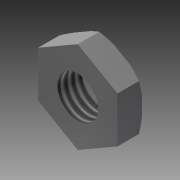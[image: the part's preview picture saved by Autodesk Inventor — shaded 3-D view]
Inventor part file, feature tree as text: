
AUTODESK INVENTOR PART (.ipt)
format: ipt  version: 2013 (Build 170138000, 138)  size: 109,056 bytes
history: native  units: mm
features: sketch x2, other x1, revolve x1, extrude x1, thread x1
ambient origin geometry x1: Origin
feature tree (6):
  other  "ソリッド1"
  revolve  "回転1"
  extrude  "押し出し1"  Depth=1.2mm
  thread  "ねじ2"
  sketch  "スケッチ1"
  sketch  "スケッチ2"
